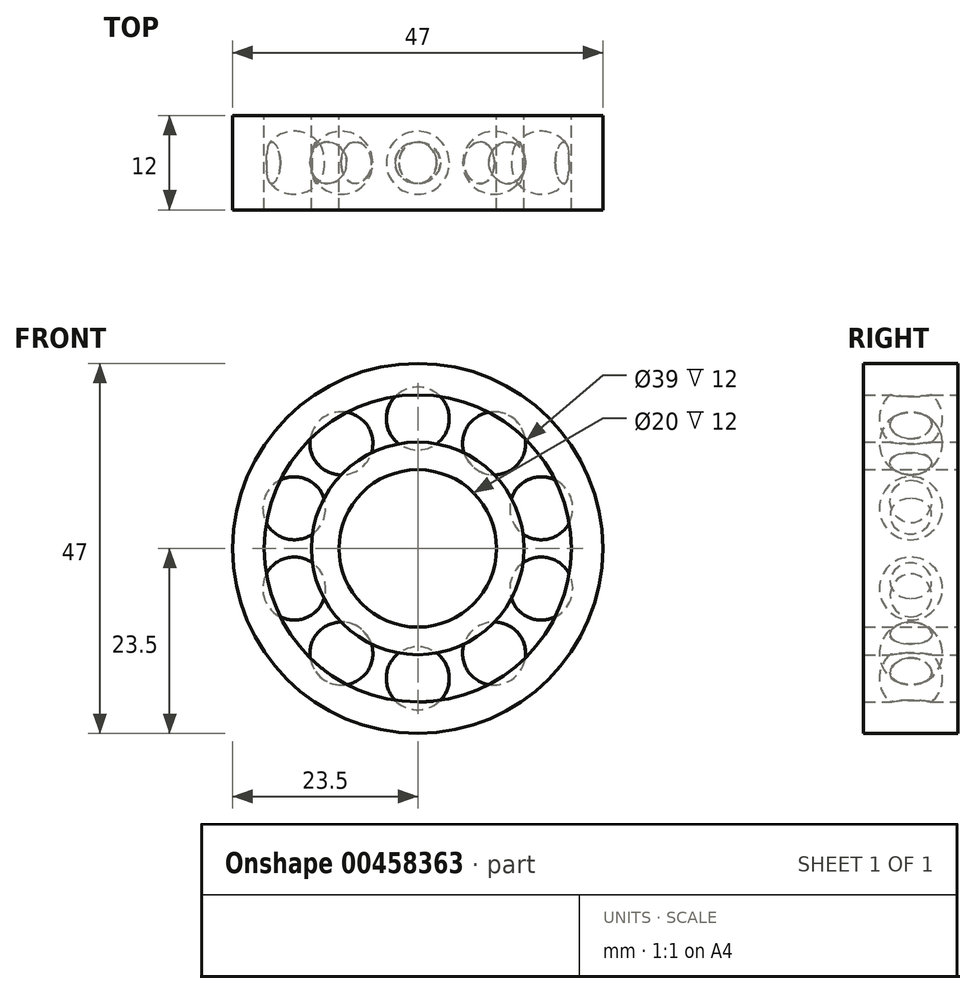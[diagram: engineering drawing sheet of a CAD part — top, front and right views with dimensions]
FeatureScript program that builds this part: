
annotation { "Feature Type Name" : "Feature", "Feature Type Description" : "" }
export const myFeature = defineFeature(function(context is Context, id is Id, definition is map)
    precondition{}
    {
        {
            var Q0;
            Q0=qCreatedBy(makeId("Front.planeOp"),FACE);
            var sketch = newSketch(context, id + "F0", { "sketchPlane" : qUnion([Q0])});
            skCircle(sketch, "E0", {"center": v(0, 0) * mm, "radius": 23.5 * mm});
            skCircle(sketch, "E1", {"center": v(0, 0) * mm, "radius": 19.5 * mm});
            skSolve(sketch);
        }
        {
            var Q0;
            Q0=qCreatedBy(makeId("Front.planeOp"),FACE);
            var sketch = newSketch(context, id + "F1", { "sketchPlane" : qUnion([Q0])});
            skCircle(sketch, "E2", {"center": v(0, 0) * mm, "radius": 13.5 * mm});
            skCircle(sketch, "E3", {"center": v(0, 0) * mm, "radius": 10 * mm});
            skSolve(sketch);
        }
        {
            var Q0;
            Q0=makeQuery(id+"F0.imprint","IMPRINT",FACE,{"disambiguationData":[TD([[makeQuery(id+"F0.imprint","IMPRINT",EDGE,{"derivedFrom":sQuery(id+"F0.wireOp",EDGE,"E0")}),1.0]])]});
            extrude(context, id + "F2", {"entities" : qUnion([Q0]), "depth" : 12 * mm, "symmetric" : true});
        }
        {
            var Q0;
            Q0=makeQuery(id+"F1.imprint","IMPRINT",FACE,{"disambiguationData":[TD([[makeQuery(id+"F1.imprint","IMPRINT",EDGE,{"derivedFrom":sQuery(id+"F1.wireOp",EDGE,"E2")}),1.0]])]});
            extrude(context, id + "F3", {"entities" : qUnion([Q0]), "depth" : 12 * mm, "symmetric" : true});
        }
        {
            var Q0;
            Q0=qCreatedBy(makeId("Front.planeOp"),FACE);
            var sketch = newSketch(context, id + "F4", { "sketchPlane" : qUnion([Q0])});
            skArc(sketch, "E4", {"start": v(0, 12.5) * mm, "mid": v(4, 16.5) * mm, "end": v(0, 20.5) * mm});
            skLineSegment(sketch, "E5", {"start": v(0, 20.5) * mm, "end": v(0, 12.5) * mm});
            skPoint(sketch, "E6.orphan", {"position": v(0, 20.86) * mm});
            skSolve(sketch);
        }
        {
            var Q0;
            Q0=makeQuery(id+"F4.imprint","IMPRINT",FACE,{"disambiguationData":[TD([[makeQuery(id+"F4.imprint","IMPRINT",EDGE,{"derivedFrom":sQuery(id+"F4.wireOp",EDGE,"E4")}),1.0]])]});
            var Q1;
            Q1=sQuery(id+"F4.wireOp",EDGE,"E5");
            revolve(context, id + "F5", {"entities" : qUnion([Q0]), "axis" : qUnion([Q1]), "revolveType" : RevolveType.FULL});
        }
        {
            var Q0;
            Q0=qCreatedBy(makeId("Right.planeOp"),FACE);
            var sketch = newSketch(context, id + "F6", { "sketchPlane" : qUnion([Q0])});
            skLineSegment(sketch, "E7", {"start": v(0, 0) * mm, "end": v(29.81, 0) * mm, "construction": true});
            skSolve(sketch);
        }
        {
            var Q0;
            Q0=makeQuery(id+"F5.opRevolve","SWEPT_BODY",BODY,{"disambiguationData":[OSD([sQuery(id+"F4.wireOp",EDGE,"E4"),sQuery(id+"F4.wireOp",EDGE,"E5")])]});
            var Q1;
            Q1=sQuery(id+"F6.wireOp",EDGE,"E7");
            circularPattern(context, id + "F7", {"operationType" : NewBodyOperationType.ADD, "entities" : qUnion([Q0]), "axis" : qUnion([Q1]), "angle" : 360 * degree, "instanceCount" : 10, "equalSpace" : true});
        }
    });
